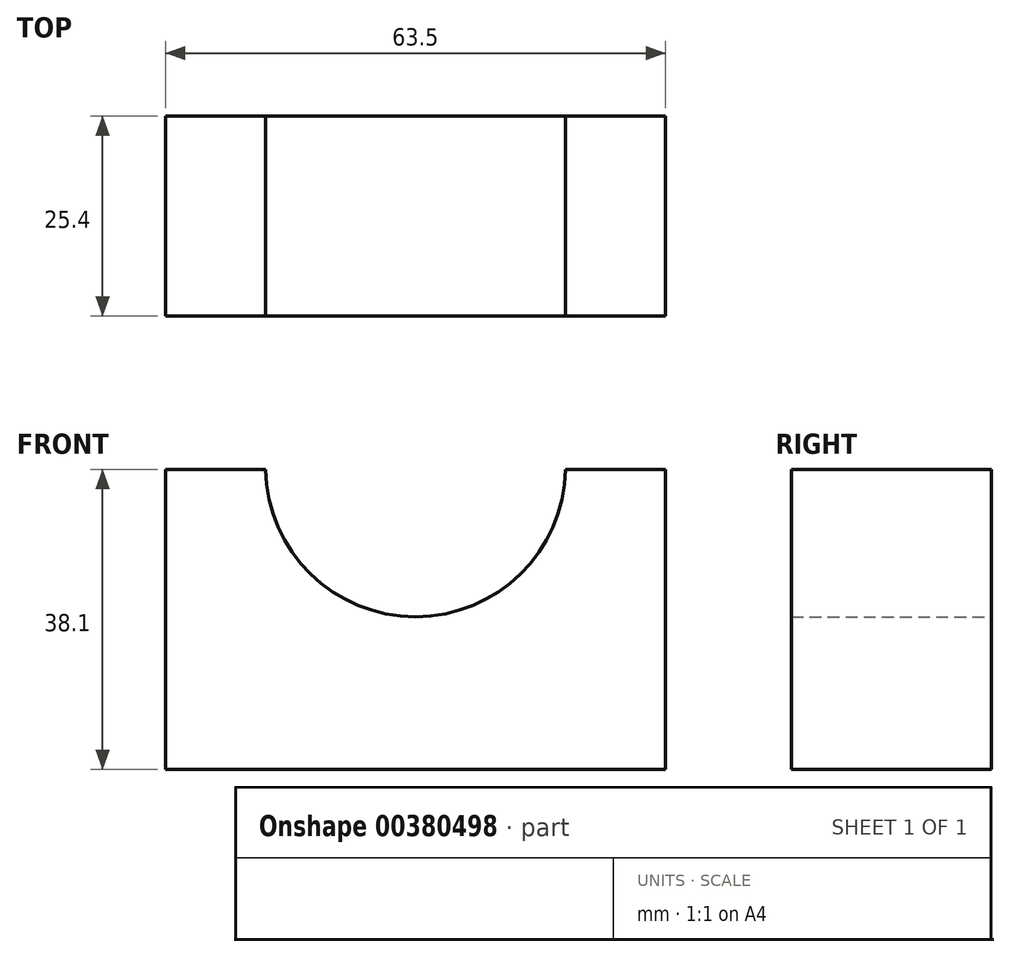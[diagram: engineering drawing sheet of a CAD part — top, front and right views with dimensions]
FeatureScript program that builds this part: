
annotation { "Feature Type Name" : "Feature", "Feature Type Description" : "" }
export const myFeature = defineFeature(function(context is Context, id is Id, definition is map)
    precondition{}
    {
        {
            var Q0;
            Q0=qCreatedBy(makeId("Front.planeOp"),FACE);
            var sketch = newSketch(context, id + "F0", { "sketchPlane" : qUnion([Q0])});
            skLineSegment(sketch, "E0", {"start": v(0, 0) * mm, "end": v(63.5, 0) * mm});
            skLineSegment(sketch, "E1", {"start": v(63.5, 0) * mm, "end": v(63.5, 38.1) * mm});
            skLineSegment(sketch, "E2", {"start": v(63.5, 38.1) * mm, "end": v(0, 38.1) * mm});
            skLineSegment(sketch, "E3", {"start": v(0, 38.1) * mm, "end": v(0, 0) * mm});
            skSolve(sketch);
        }
        {
            var Q0;
            Q0=makeQuery(id+"F0.imprint","IMPRINT",FACE,{"disambiguationData":[TD([[makeQuery(id+"F0.imprint","IMPRINT",EDGE,{"derivedFrom":sQuery(id+"F0.wireOp",EDGE,"E0")}),1.0]])]});
            var sketch = newSketch(context, id + "F1", { "sketchPlane" : qUnion([Q0])});
            skArc(sketch, "E4", {"start": v(12.7, 38.3) * mm, "mid": v(31.89, 19.4) * mm, "end": v(50.8, 38.58) * mm});
            skSolve(sketch);
        }
        {
            var Q0;
            Q0=makeQuery(id+"F0.imprint","IMPRINT",FACE,{"disambiguationData":[TD([[makeQuery(id+"F0.imprint","IMPRINT",EDGE,{"derivedFrom":sQuery(id+"F0.wireOp",EDGE,"E0")}),1.0]])]});
            extrude(context, id + "F2", {"entities" : qUnion([Q0]), "depth" : 25.4 * mm});
        }
        {
            var Q0;
            {var subQ0=sQuery(id+"F1.wireOp",EDGE,"E4");var subQ1=makeQuery(id+"F0.imprint","IMPRINT",EDGE,{"derivedFrom":sQuery(id+"F0.wireOp",EDGE,"E2")});var subQ2=makeQuery(id+"F1.imprint","INTERSECT",VERTEX,{"disambiguationData":[OD(0.0)],"derivedFrom":[subQ1,subQ0]});Q0=makeQuery(id+"F1.imprint","IMPRINT",FACE,{"disambiguationData":[TD([[makeQuery(id+"F1.imprint","IMPRINT",EDGE,{"disambiguationData":[TD([[subQ2,1.0]])],"derivedFrom":subQ0}),1.0]])]});}
            extrude(context, id + "F3", {"entities" : qUnion([Q0]), "operationType" : NewBodyOperationType.REMOVE, "depth" : 25.4 * mm});
        }
    });
